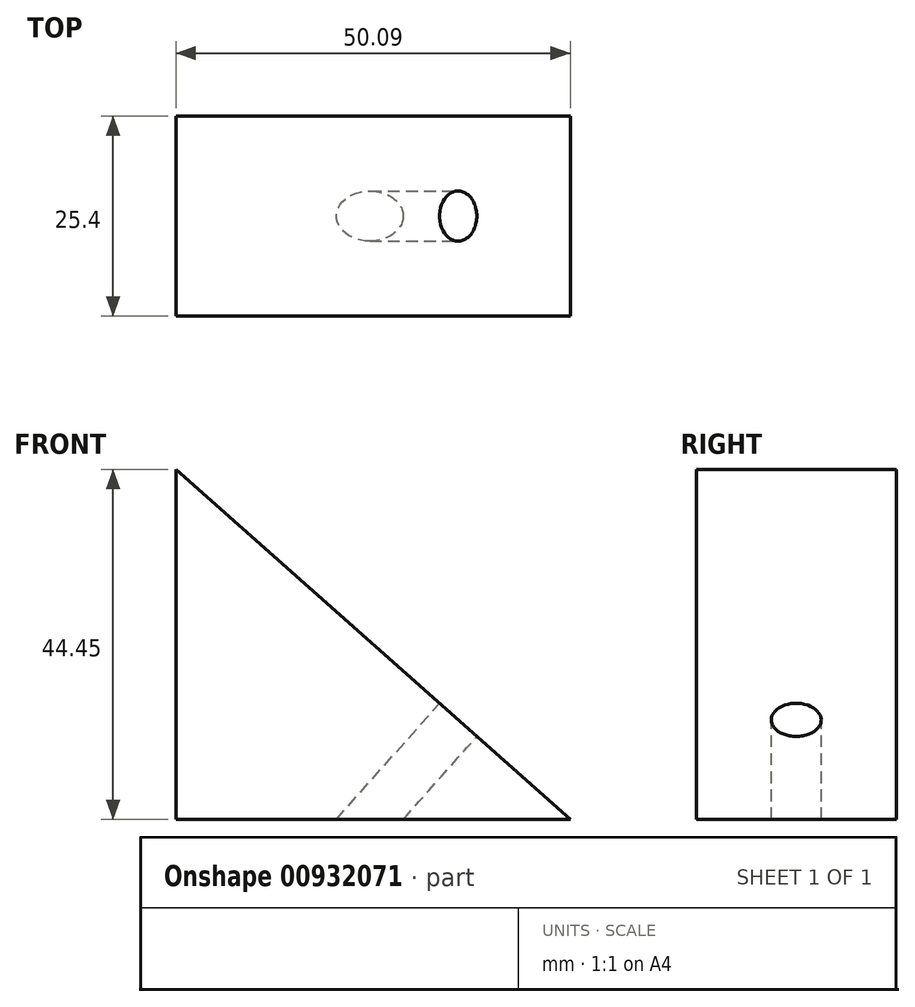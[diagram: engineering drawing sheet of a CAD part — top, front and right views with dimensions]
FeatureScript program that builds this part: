
annotation { "Feature Type Name" : "Feature", "Feature Type Description" : "" }
export const myFeature = defineFeature(function(context is Context, id is Id, definition is map)
    precondition{}
    {
        {
            var Q0;
            Q0=qCreatedBy(makeId("Front.planeOp"),FACE);
            var sketch = newSketch(context, id + "F0", { "sketchPlane" : qUnion([Q0])});
            skLineSegment(sketch, "E0", {"start": v(0, 0) * mm, "end": v(0, 44.45) * mm});
            skLineSegment(sketch, "E1", {"start": v(0, 44.45) * mm, "end": v(50.09, 0) * mm});
            skLineSegment(sketch, "E2", {"start": v(50.09, 0) * mm, "end": v(0, 0) * mm});
            skSolve(sketch);
        }
        {
            var Q0;
            Q0 = qSketchRegion(id + "F0", true);
            extrude(context, id + "F1", {"entities" : qUnion([Q0]), "depth" : 25.4 * mm, "offsetDistance" : 25.4 * mm});
        }
        {
            var Q0;
            Q0=makeQuery(id+"F1.opExtrude","SWEPT_FACE",FACE,{"disambiguationData":[OSD([sQuery(id+"F0.wireOp",EDGE,"E1")])]});
            var sketch = newSketch(context, id + "F2", { "sketchPlane" : qUnion([Q0])});
            skCircle(sketch, "E3", {"center": v(18.41, -12.7) * mm, "radius": 3.18 * mm});
            skLineSegment(sketch, "E4", {"start": v(37.46, -12.7) * mm, "end": v(18.41, -12.7) * mm, "construction": true});
            skSolve(sketch);
        }
        {
            var Q0;
            Q0 = qSketchRegion(id + "F2", true);
            extrude(context, id + "F3", {"entities" : qUnion([Q0]), "operationType" : NewBodyOperationType.REMOVE, "oppositeDirection" : true, "depth" : 25.4 * mm, "offsetDistance" : 25.4 * mm});
        }
    });
